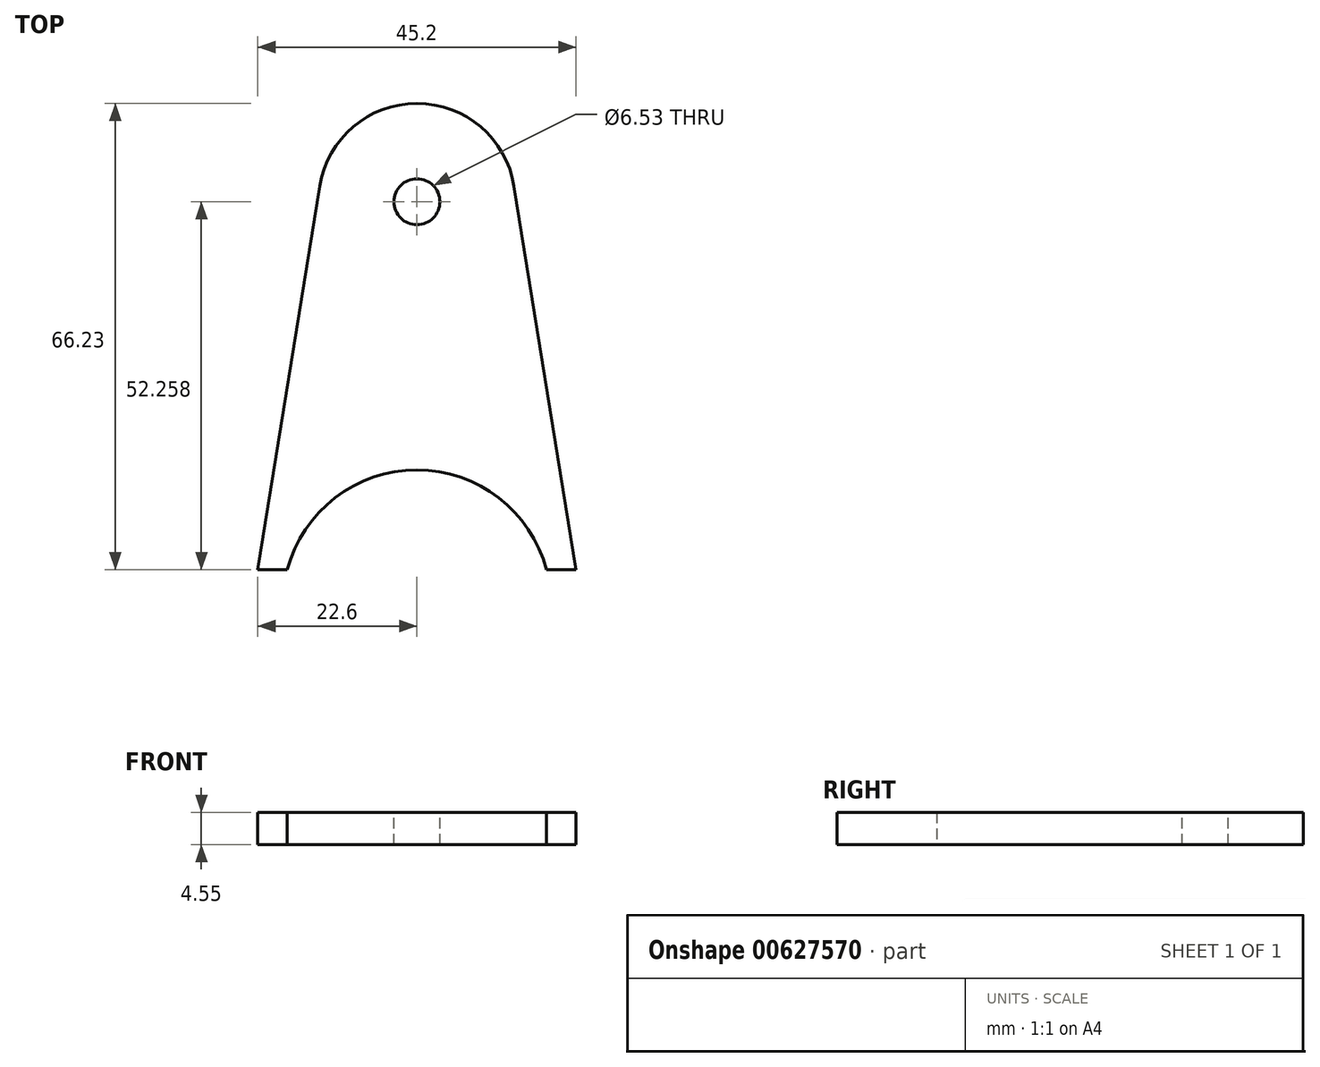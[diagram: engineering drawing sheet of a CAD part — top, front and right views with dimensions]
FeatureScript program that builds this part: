
annotation { "Feature Type Name" : "Feature", "Feature Type Description" : "" }
export const myFeature = defineFeature(function(context is Context, id is Id, definition is map)
    precondition{}
    {
        {
            var Q0;
            Q0=qCreatedBy(makeId("Top.planeOp"),FACE);
            var sketch = newSketch(context, id + "F0", { "sketchPlane" : qUnion([Q0])});
            skLineSegment(sketch, "E0", {"start": v(0, -49.37) * mm, "end": v(0, 65.55) * mm, "construction": true});
            skArc(sketch, "E1", {"start": v(0, 31) * mm, "mid": v(-9.06, 27.68) * mm, "end": v(-13.8, 19.27) * mm});
            skArc(sketch, "E2", {"start": v(0, -21.06) * mm, "mid": v(-11.61, -25.01) * mm, "end": v(-18.41, -35.22) * mm});
            skLineSegment(sketch, "E3", {"start": v(-22.6, -35.22) * mm, "end": v(-13.8, 19.27) * mm});
            skArc(sketch, "E4.MirrorCS", {"start": v(0, 31) * mm, "mid": v(9.06, 27.68) * mm, "end": v(13.8, 19.27) * mm});
            skLineSegment(sketch, "E5.MirrorCS", {"start": v(22.6, -35.22) * mm, "end": v(13.8, 19.27) * mm});
            skArc(sketch, "E6.MirrorCS", {"start": v(0, -21.06) * mm, "mid": v(11.61, -25.01) * mm, "end": v(18.41, -35.22) * mm});
            skLineSegment(sketch, "E7", {"start": v(-22.6, -35.22) * mm, "end": v(-18.41, -35.22) * mm});
            skLineSegment(sketch, "E8", {"start": v(18.41, -35.22) * mm, "end": v(22.6, -35.22) * mm});
            skSolve(sketch);
        }
        {
            var Q0;
            Q0=qSketchRegion(id+"F0",true);
            extrude(context, id + "F1", {"entities" : qUnion([Q0]), "depth" : 4.55 * mm, "offsetDistance" : 25.4 * mm});
        }
        {
            var Q0;
            Q0=makeQuery(id+"F1.opExtrude","CAP_FACE",FACE,{"disambiguationData":[OSD([sQuery(id+"F0.wireOp",EDGE,"E1"),sQuery(id+"F0.wireOp",EDGE,"E2"),sQuery(id+"F0.wireOp",EDGE,"E3"),sQuery(id+"F0.wireOp",EDGE,"E4.MirrorCS"),sQuery(id+"F0.wireOp",EDGE,"E5.MirrorCS"),sQuery(id+"F0.wireOp",EDGE,"E6.MirrorCS"),sQuery(id+"F0.wireOp",EDGE,"rgRoUT8c-bVL2-FPYU-7MTc-vp1h9EsBAV6d"),sQuery(id+"F0.wireOp",EDGE,"05189ca0-4bbf-4e7c-aff5-e242d629c5390.MirrorCS")])],"isStart":false});
            var sketch = newSketch(context, id + "F2", { "sketchPlane" : qUnion([Q0])});
            skPoint(sketch, "E9", {"position": v(0, 17.04) * mm});
            skSolve(sketch);
        }
        {
            var Q0;
            Q0=sQuery(id+"F2.wireOp",VERTEX,"E9");
            var Q1;
            Q1=makeQuery(id+"F1.opExtrude","SWEPT_BODY",BODY,{"disambiguationData":[OSD([sQuery(id+"F0.wireOp",EDGE,"E1"),sQuery(id+"F0.wireOp",EDGE,"E2"),sQuery(id+"F0.wireOp",EDGE,"E3"),sQuery(id+"F0.wireOp",EDGE,"E4.MirrorCS"),sQuery(id+"F0.wireOp",EDGE,"E5.MirrorCS"),sQuery(id+"F0.wireOp",EDGE,"E6.MirrorCS"),sQuery(id+"F0.wireOp",EDGE,"rgRoUT8c-bVL2-FPYU-7MTc-vp1h9EsBAV6d"),sQuery(id+"F0.wireOp",EDGE,"05189ca0-4bbf-4e7c-aff5-e242d629c5390.MirrorCS")])]});
            hole(context, id + "F3", {"style" : HoleStyle.SIMPLE, "endStyle" : HoleEndStyle.THROUGH, "standardTappedOrClearance" : lookupTablePath({ "standard" : "ANSI", "fit" : "Close", "size" : "1/4", "type" : "Clearance" }), "standardBlindInLast" : lookupTablePath({ "fit" : "Close", "standard" : "ANSI", "size" : "1/4", "type" : "Clearance" }), "holeDiameter" : 6.53 * mm, "isTappedThrough" : true, "tappedDepth" : 12.7 * mm, "tapClearance" : 3, "locations" : qUnion([Q0]), "scope" : qUnion([Q1]), "majorDiameter" : 6.35 * mm});
        }
    });
